# Revit family: Door-Out-Swing-Pella-Architect-Contemporary-Double3
name_source: partatom
category: Doors
revit_build: Autodesk Revit Architecture 2013 (Build: 20130531_2115(x64)
units: mm (PartAtom-declared; Revit-internal decimal feet)

## types (1)
- default load type catalog
    Assembly Code = B2030130
    Center Thickness = 0' - 1 11/16"
    Description = Outswing Patio Door
    Energy Star = http://www.pella.com
    Exterior Finish = Aluminum-Pella-EnduraClad-White
    Fixed Panel = Yes
    Frame Projection Ext. = 0' - 1"
    Frame Projection Int. = 0' - 1"
    Frame Width = 0' - 3"
    Function = Interior
    Glass = Glass-Pella-Low_E-Argon
    Glass Thickness = 0' - 0 13/16"
    Grille Height = 6' - 11 13/16"
    Grille Width = 0' - 0 7/8"
    Height = 8' - 0"
    Horizontal Grille Offset = 2' - 3 15/16"
    Horizontal Grille Spacing = 2' - 3 15/16"
    Horizontal Mullions = 2
    Inset = 0' - 0"
    Interior Finish = Wood-Pella-Pine
    Interior Sill = Wood-Pella-Interior_Sill
    Jamb Extensions = Yes
    Manufacturer = Pella
    Max Height = 9' - 11 1/2"
    Max Lites = 10
    Max Width = 6' - 3"
    Min Height = 6' - 7 1/2"
    Min Width = 4' - 2"
    Model = Contemporary Outswing Active/Fixed
    Nail Fin = Yes
    Offset = 0' - 0"
    Operation = Outswing
    Panel Grille Width = 2' - 0 3/4"
    Panel Height = 7' - 9 5/8"
    Panel Width = 2' - 9 15/16"
    Prairie Grille = No
    Prairie Offset = 0' - 3 11/16"
    Product Documentation Link = http://media.pella.com
    Product Name = Architect Series
    Product Page URL = http://professional.pella.com
    Requested Height = 8' - 0"
    Requested Width = 6' - 0"
    Rough Height = 8' - 0 3/4"
    Rough Width = 6' - 0 3/4"
    Second Panel Operable = No
    Sill Height = 0' - 5 7/8"
    Specification = http://media.pella.com
    Thickness = 0' - 5 7/8"
    Traditioinal Grille Single Horizontal = No
    Traditional Grille = No
    Traditional Grille Horizontal Array = No
    Traditional Grille Single Vertical = No
    Traditional Grille Vertical Array = No
    Traditional Lites High = 2
    Traditional Lites Wide = 2
    Trim = Yes
    Type Comments = Active/Fixed
    URL = http://professional.pella.com
    Vertical Grille Offset = 0' - 8 1/4"
    Vertical Grille Spacing = 0' - 8 1/4"
    Vertical Mullions = 2
    Wall Closure = By host
    Warranty = https://content.pella.com
    Width = 6' - 0"

## geometry (parser evidence)
native form markers: Blend x34, Sweep x10
no freeform markers — native parametric forms only
